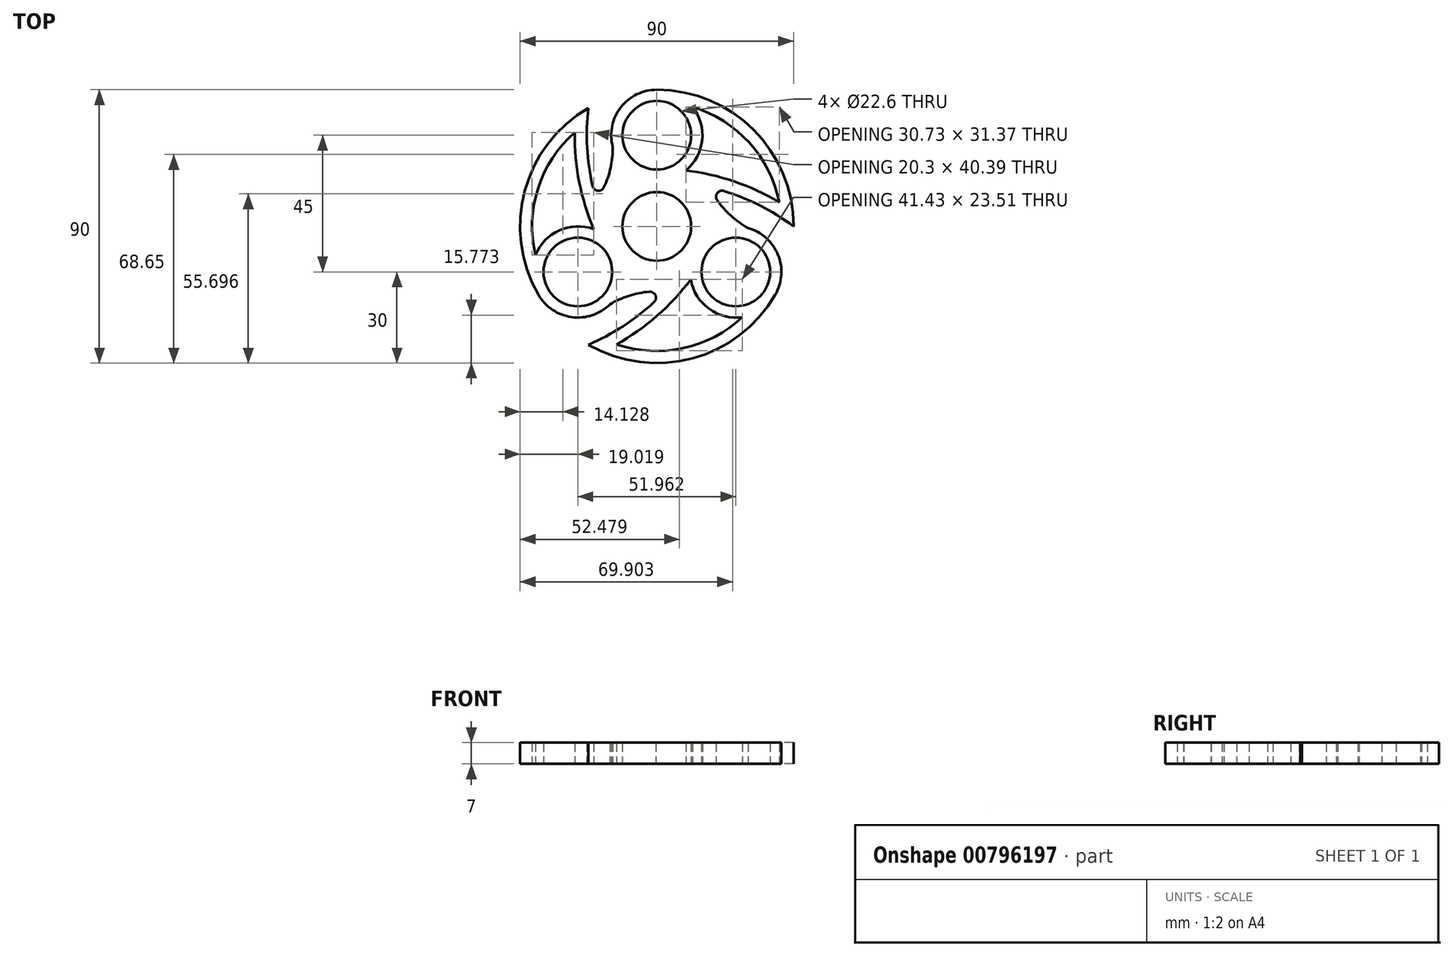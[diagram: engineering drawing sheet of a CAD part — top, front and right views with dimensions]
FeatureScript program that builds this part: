
annotation { "Feature Type Name" : "Feature", "Feature Type Description" : "" }
export const myFeature = defineFeature(function(context is Context, id is Id, definition is map)
    precondition{}
    {
        {
            var Q0;
            Q0=qCreatedBy(makeId("Top.planeOp"),FACE);
            var sketch = newSketch(context, id + "F0", { "sketchPlane" : qUnion([Q0])});
            skLineSegment(sketch, "E0", {"start": v(0, 0) * mm, "end": v(0, 30) * mm, "construction": true});
            skCircle(sketch, "E1", {"center": v(0, 0) * mm, "radius": 30 * mm, "construction": true});
            skLineSegment(sketch, "E2", {"start": v(0, 30) * mm, "end": v(0, 45) * mm, "construction": true});
            skLineSegment(sketch, "E3", {"start": v(0, 0) * mm, "end": v(45, 0) * mm, "construction": true});
            skLineSegment(sketch, "E4.1.0", {"start": v(0, 0) * mm, "end": v(-25.98, -15) * mm, "construction": true});
            skLineSegment(sketch, "E4.2.0", {"start": v(0, 0) * mm, "end": v(25.98, -15) * mm, "construction": true});
            skCircle(sketch, "E5", {"center": v(0, 30) * mm, "radius": 15 * mm});
            skLineSegment(sketch, "E6", {"start": v(0, 15) * mm, "end": v(-19.55, 15) * mm, "construction": true});
            skLineSegment(sketch, "E7", {"start": v(0, 45) * mm, "end": v(-19.24, 45) * mm, "construction": true});
            skCircle(sketch, "E8", {"center": v(-25.98, -15) * mm, "radius": 15 * mm, "construction": true});
            skArc(sketch, "E9", {"start": v(-17.4, 12.88) * mm, "mid": v(-15.19, 19.4) * mm, "end": v(-14.52, 26.25) * mm});
            skCircle(sketch, "E10", {"center": v(0, 0) * mm, "radius": 45 * mm, "construction": true});
            skArc(sketch, "E11", {"start": v(0, 45) * mm, "mid": v(31.82, 31.82) * mm, "end": v(45, 0) * mm});
            skArc(sketch, "E12", {"start": v(22.09, 11.67) * mm, "mid": v(34.05, 6.83) * mm, "end": v(45, 0) * mm});
            skArc(sketch, "E13.1.1", {"start": v(-38.97, -22.5) * mm, "mid": v(-43.47, 11.65) * mm, "end": v(-22.5, 38.97) * mm});
            skArc(sketch, "E13.1.2", {"start": v(-21.15, 13.3) * mm, "mid": v(-22.94, 26.07) * mm, "end": v(-22.5, 38.97) * mm});
            skCircle(sketch, "E13.1.4", {"center": v(-25.98, -15) * mm, "radius": 11.3 * mm});
            skCircle(sketch, "E13.1.5", {"center": v(-25.98, -15) * mm, "radius": 15 * mm});
            skArc(sketch, "E13.1.6", {"start": v(-2.46, -21.5) * mm, "mid": v(-9.2, -22.85) * mm, "end": v(-15.47, -25.7) * mm});
            skArc(sketch, "E13.2.1", {"start": v(38.97, -22.5) * mm, "mid": v(11.65, -43.47) * mm, "end": v(-22.5, -38.97) * mm});
            skArc(sketch, "E13.2.2", {"start": v(-0.93, -24.97) * mm, "mid": v(-11.11, -32.9) * mm, "end": v(-22.5, -38.97) * mm});
            skCircle(sketch, "E13.2.4", {"center": v(25.98, -15) * mm, "radius": 11.3 * mm});
            skCircle(sketch, "E13.2.5", {"center": v(25.98, -15) * mm, "radius": 15 * mm});
            skArc(sketch, "E13.2.6", {"start": v(19.85, 8.62) * mm, "mid": v(24.4, 3.45) * mm, "end": v(30, -0.55) * mm});
            skPoint(sketch, "E14.newPointA", {"position": v(0, 15) * mm});
            skPoint(sketch, "E14.newPointB", {"position": v(14.52, 26.25) * mm});
            skArc(sketch, "E14.filletArc", {"start": v(22.09, 11.67) * mm, "mid": v(19.89, 10.94) * mm, "end": v(19.85, 8.62) * mm});
            skPoint(sketch, "E15.newPointA", {"position": v(-30, -0.55) * mm});
            skPoint(sketch, "E15.newPointB", {"position": v(-13, -7.5) * mm});
            skArc(sketch, "E15.filletArc", {"start": v(-21.15, 13.3) * mm, "mid": v(-19.42, 11.75) * mm, "end": v(-17.4, 12.88) * mm});
            skPoint(sketch, "E16.newPointA", {"position": v(15.47, -25.7) * mm});
            skPoint(sketch, "E16.newPointB", {"position": v(13, -7.5) * mm});
            skArc(sketch, "E16.filletArc", {"start": v(-0.93, -24.97) * mm, "mid": v(-0.47, -22.7) * mm, "end": v(-2.46, -21.5) * mm});
            skArc(sketch, "E17", {"start": v(0, 41.05) * mm, "mid": v(-28, -30.01) * mm, "end": v(40.95, 2.83) * mm, "construction": true});
            skArc(sketch, "E18.0", {"start": v(9.54, 18.42) * mm, "mid": v(25.45, 14.79) * mm, "end": v(40.27, 7.97) * mm});
            skArc(sketch, "E19.trimOffspring", {"start": v(40.27, 7.97) * mm, "mid": v(30.37, 27.62) * mm, "end": v(11.74, 39.34) * mm});
            skArc(sketch, "E20.1.0", {"start": v(-27.03, 30.9) * mm, "mid": v(-39.1, 12.5) * mm, "end": v(-39.94, -9.5) * mm});
            skArc(sketch, "E20.1.1", {"start": v(-20.72, -0.95) * mm, "mid": v(-25.53, 14.64) * mm, "end": v(-27.03, 30.9) * mm});
            skArc(sketch, "E20.2.0", {"start": v(-13.24, -38.86) * mm, "mid": v(8.73, -40.11) * mm, "end": v(28.2, -29.84) * mm});
            skArc(sketch, "E20.2.1", {"start": v(11.19, -17.47) * mm, "mid": v(0.09, -29.43) * mm, "end": v(-13.24, -38.86) * mm});
            skCircle(sketch, "E21", {"center": v(0, 0) * mm, "radius": 11.3 * mm});
            skCircle(sketch, "E22", {"center": v(0, 30) * mm, "radius": 11.3 * mm});
            skSolve(sketch);
        }
        {
            var Q0;
            Q0=qSketchRegion(id+"F0",true);
            extrude(context, id + "F1", {"entities" : qUnion([Q0]), "depth" : 7 * mm, "offsetDistance" : 25 * mm});
        }
    });
